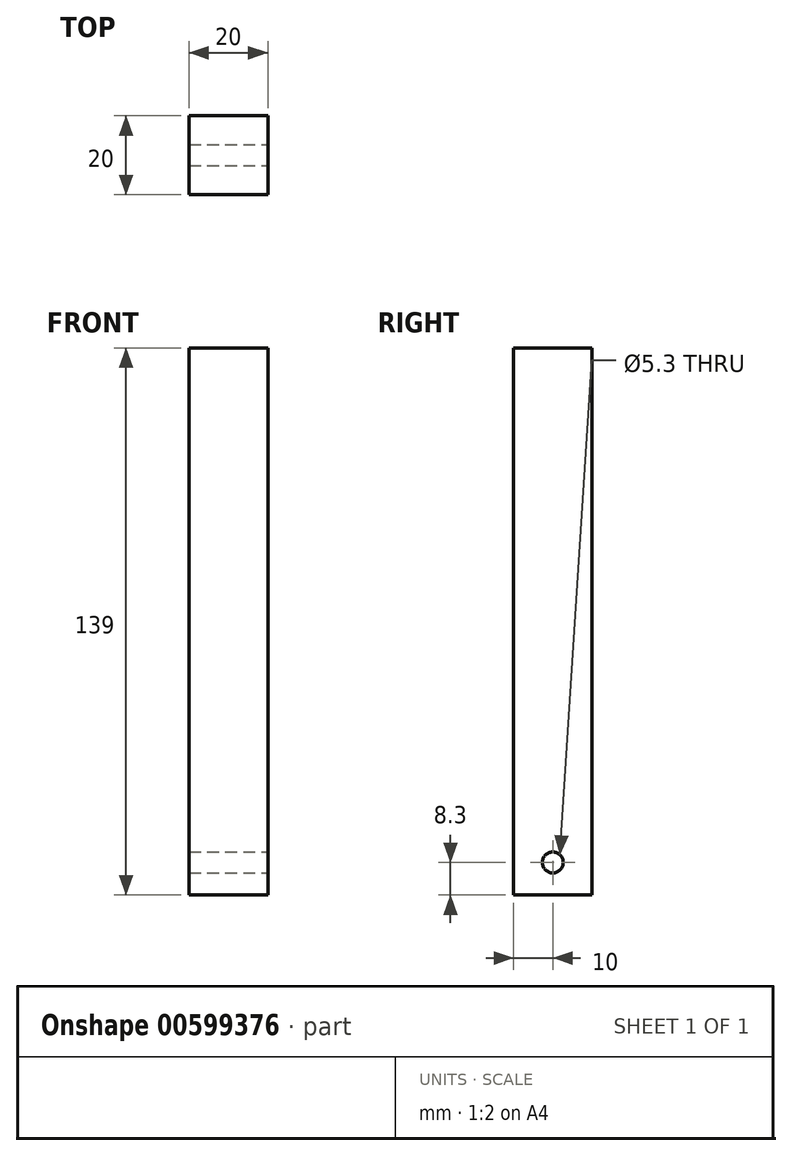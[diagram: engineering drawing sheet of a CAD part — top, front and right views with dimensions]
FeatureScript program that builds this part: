
annotation { "Feature Type Name" : "Feature", "Feature Type Description" : "" }
export const myFeature = defineFeature(function(context is Context, id is Id, definition is map)
    precondition{}
    {
        {
            var Q0;
            Q0=qCreatedBy(makeId("Top.planeOp"),FACE);
            var sketch = newSketch(context, id + "F0", { "sketchPlane" : qUnion([Q0])});
            skLineSegment(sketch, "E0.bottom", {"start": v(-10, 10) * mm, "end": v(10, 10) * mm});
            skLineSegment(sketch, "E0.top", {"start": v(-10, -10) * mm, "end": v(10, -10) * mm});
            skLineSegment(sketch, "E0.left", {"start": v(-10, 10) * mm, "end": v(-10, -10) * mm});
            skLineSegment(sketch, "E0.right", {"start": v(10, 10) * mm, "end": v(10, -10) * mm});
            skSolve(sketch);
        }
        {
            var Q0;
            Q0=qSketchRegion(id+"F0",true);
            extrude(context, id + "F1", {"entities" : qUnion([Q0]), "depth" : 139 * mm});
        }
        {
            var Q0;
            Q0=makeQuery(id+"F1.opExtrude","SWEPT_FACE",FACE,{"disambiguationData":[OSD([sQuery(id+"F0.wireOp",EDGE,"E0.right")])]});
            var sketch = newSketch(context, id + "F2", { "sketchPlane" : qUnion([Q0])});
            skCircle(sketch, "E1", {"center": v(0, 10) * mm, "radius": 2.5 * mm});
            skSolve(sketch);
        }
        {
            var Q0;
            Q0=makeQuery(id+"F2.imprint","IMPRINT",FACE,{"disambiguationData":[TD([[makeQuery(id+"F2.imprint","IMPRINT",EDGE,{"derivedFrom":sQuery(id+"F2.wireOp",EDGE,"E1")}),-1.0]])]});
            var sketch = newSketch(context, id + "F3", { "sketchPlane" : qUnion([Q0])});
            skCircle(sketch, "E2", {"center": v(0, 8.3) * mm, "radius": 2.65 * mm});
            skSolve(sketch);
        }
        {
            var Q0;
            Q0=qSketchRegion(id+"F3",true);
            extrude(context, id + "F4", {"entities" : qUnion([Q0]), "operationType" : NewBodyOperationType.REMOVE, "endBound" : BoundingType.THROUGH_ALL, "oppositeDirection" : true, "depth" : 25 * mm});
        }
    });
